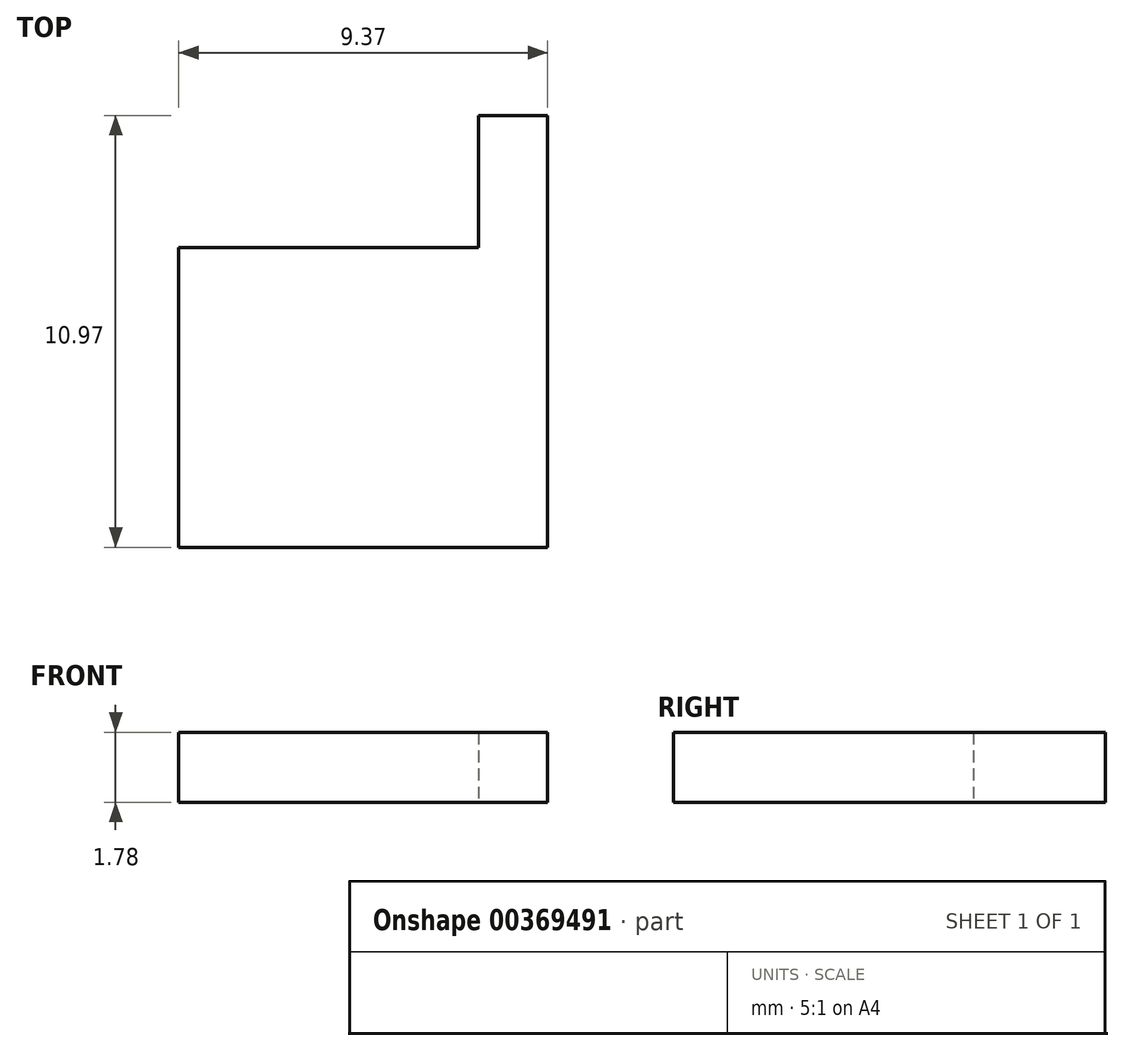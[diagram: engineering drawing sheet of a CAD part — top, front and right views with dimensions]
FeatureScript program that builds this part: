
annotation { "Feature Type Name" : "Feature", "Feature Type Description" : "" }
export const myFeature = defineFeature(function(context is Context, id is Id, definition is map)
    precondition{}
    {
        {
            var Q0;
            Q0=qCreatedBy(makeId("Top.planeOp"),FACE);
            var sketch = newSketch(context, id + "F0", { "sketchPlane" : qUnion([Q0])});
            skLineSegment(sketch, "E0.bottom", {"start": v(0, 0) * mm, "end": v(7.62, 0) * mm});
            skLineSegment(sketch, "E0.top", {"start": v(0, 7.62) * mm, "end": v(7.62, 7.62) * mm});
            skLineSegment(sketch, "E0.left", {"start": v(0, 0) * mm, "end": v(0, 7.62) * mm});
            skLineSegment(sketch, "E0.right", {"start": v(7.62, 0) * mm, "end": v(7.62, 7.62) * mm});
            skLineSegment(sketch, "E1.bottom", {"start": v(7.62, 0) * mm, "end": v(9.37, 0) * mm});
            skLineSegment(sketch, "E1.top", {"start": v(7.62, 10.97) * mm, "end": v(9.37, 10.97) * mm});
            skLineSegment(sketch, "E1.left", {"start": v(7.62, 0) * mm, "end": v(7.62, 10.97) * mm});
            skLineSegment(sketch, "E1.right", {"start": v(9.37, 0) * mm, "end": v(9.37, 10.97) * mm});
            skSolve(sketch);
        }
        {
            var Q0;
            Q0 = qSketchRegion(id + "F0", true);
            extrude(context, id + "F1", {"entities" : qUnion([Q0]), "depth" : 1.78 * mm});
        }
    });
